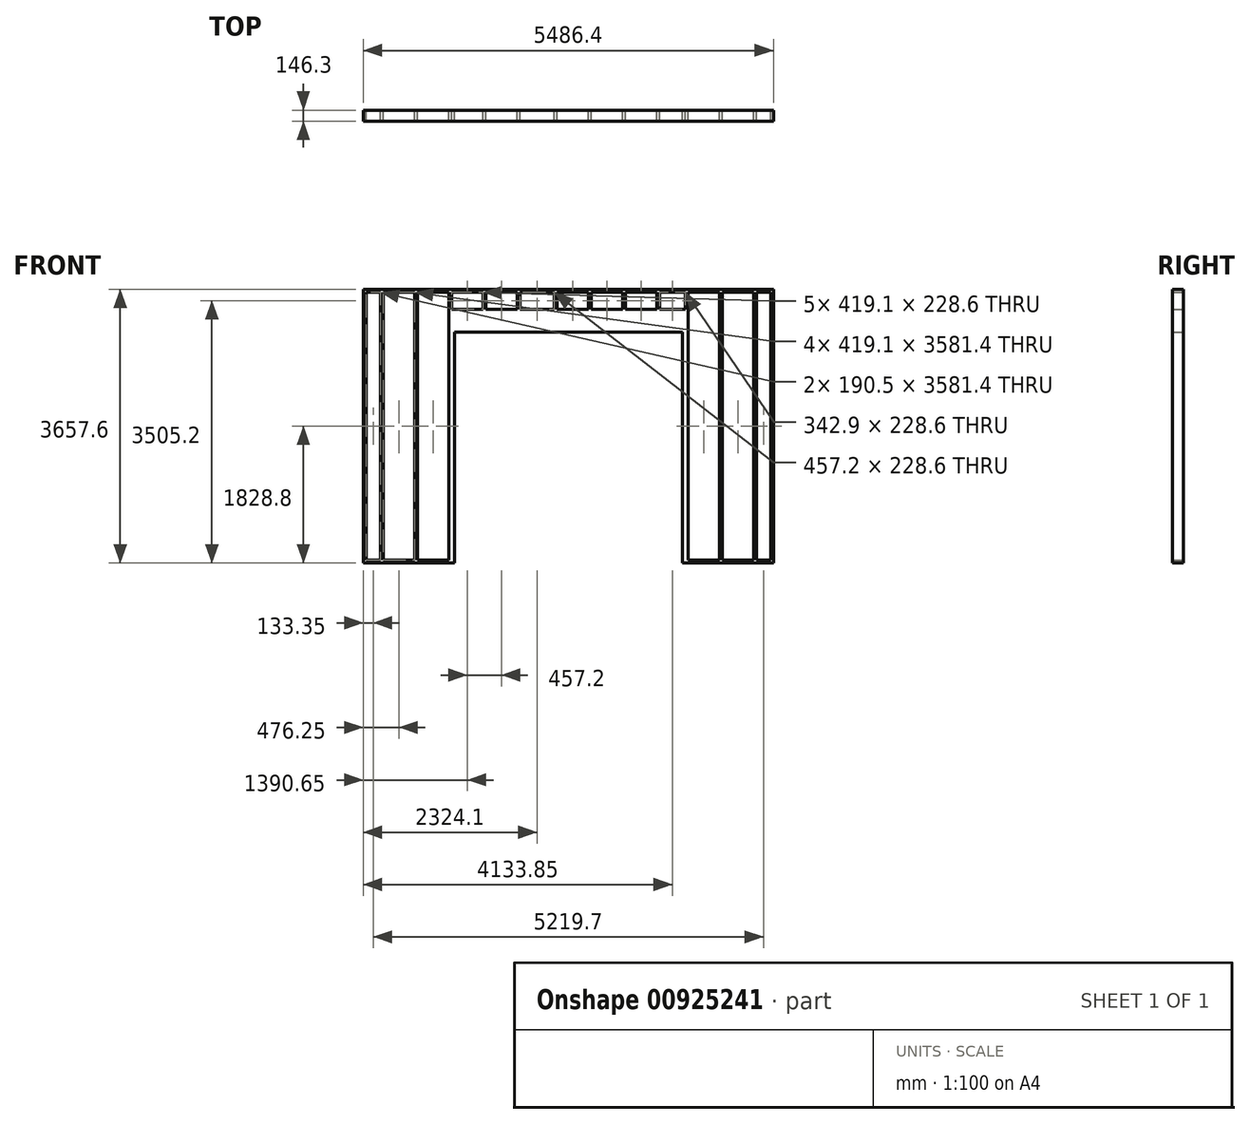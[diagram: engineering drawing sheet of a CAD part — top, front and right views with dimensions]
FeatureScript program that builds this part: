
annotation { "Feature Type Name" : "Feature", "Feature Type Description" : "" }
export const myFeature = defineFeature(function(context is Context, id is Id, definition is map)
    precondition{}
    {
        {
            var Q0;
            Q0=qCreatedBy(makeId("Front.planeOp"),FACE);
            var sketch = newSketch(context, id + "F0", { "sketchPlane" : qUnion([Q0])});
            skLineSegment(sketch, "E0.bottom", {"start": v(822.96, 0) * mm, "end": v(2042.16, 0) * mm});
            skLineSegment(sketch, "E0.top", {"start": v(822.96, 3657.6) * mm, "end": v(6309.36, 3657.6) * mm});
            skLineSegment(sketch, "E1.1.0.0", {"start": v(822.96, 3619.5) * mm, "end": v(822.96, 38.1) * mm});
            skLineSegment(sketch, "E1.1.0.1", {"start": v(861.06, 3619.5) * mm, "end": v(861.06, 38.1) * mm});
            skLineSegment(sketch, "E1.2.0.0", {"start": v(1051.56, 3619.5) * mm, "end": v(1051.56, 38.1) * mm});
            skLineSegment(sketch, "E1.2.0.1", {"start": v(1089.66, 3619.5) * mm, "end": v(1089.66, 38.1) * mm});
            skLineSegment(sketch, "E1.3.0.0", {"start": v(1508.76, 3619.5) * mm, "end": v(1508.76, 38.1) * mm});
            skLineSegment(sketch, "E1.3.0.1", {"start": v(1546.86, 3619.5) * mm, "end": v(1546.86, 38.1) * mm});
            skLineSegment(sketch, "E1.4.0.0", {"start": v(1965.96, 3619.5) * mm, "end": v(1965.96, 38.1) * mm});
            skLineSegment(sketch, "E1.4.0.1", {"start": v(2004.06, 3619.5) * mm, "end": v(2004.06, 3390.9) * mm});
            skLineSegment(sketch, "E1.5.0.0", {"start": v(2423.16, 3619.5) * mm, "end": v(2423.16, 3390.9) * mm});
            skLineSegment(sketch, "E1.5.0.1", {"start": v(2461.26, 3619.5) * mm, "end": v(2461.26, 3390.9) * mm});
            skLineSegment(sketch, "E1.6.0.0", {"start": v(2880.36, 3619.5) * mm, "end": v(2880.36, 3390.9) * mm});
            skLineSegment(sketch, "E1.6.0.1", {"start": v(2918.46, 3619.5) * mm, "end": v(2918.46, 3390.9) * mm});
            skLineSegment(sketch, "E1.7.0.0", {"start": v(3375.66, 3619.5) * mm, "end": v(3375.66, 3390.9) * mm});
            skLineSegment(sketch, "E1.7.0.1", {"start": v(3413.76, 3619.5) * mm, "end": v(3413.76, 3390.9) * mm});
            skLineSegment(sketch, "E1.8.0.0", {"start": v(3832.86, 3619.5) * mm, "end": v(3832.86, 3390.9) * mm});
            skLineSegment(sketch, "E1.8.0.1", {"start": v(3870.96, 3619.5) * mm, "end": v(3870.96, 3390.9) * mm});
            skLineSegment(sketch, "E1.9.0.0", {"start": v(4290.06, 3619.5) * mm, "end": v(4290.06, 3390.9) * mm});
            skLineSegment(sketch, "E1.9.0.1", {"start": v(4328.16, 3619.5) * mm, "end": v(4328.16, 3390.9) * mm});
            skLineSegment(sketch, "E1.10.0.0", {"start": v(4747.26, 3619.5) * mm, "end": v(4747.26, 3390.9) * mm});
            skLineSegment(sketch, "E1.10.0.1", {"start": v(4785.36, 3619.5) * mm, "end": v(4785.36, 3390.9) * mm});
            skLineSegment(sketch, "E1.11.0.0", {"start": v(5128.26, 3619.5) * mm, "end": v(5128.26, 3390.9) * mm});
            skLineSegment(sketch, "E1.11.0.1", {"start": v(5166.36, 3619.5) * mm, "end": v(5166.36, 38.1) * mm});
            skLineSegment(sketch, "E1.12.0.0", {"start": v(5585.46, 3619.5) * mm, "end": v(5585.46, 38.1) * mm});
            skLineSegment(sketch, "E1.12.0.1", {"start": v(5623.56, 3619.5) * mm, "end": v(5623.56, 38.1) * mm});
            skLineSegment(sketch, "E1.13.0.0", {"start": v(6042.66, 3619.5) * mm, "end": v(6042.66, 38.1) * mm});
            skLineSegment(sketch, "E1.13.0.1", {"start": v(6080.76, 3619.5) * mm, "end": v(6080.76, 38.1) * mm});
            skLineSegment(sketch, "E1.14.0.0", {"start": v(6271.26, 3619.5) * mm, "end": v(6271.26, 38.1) * mm});
            skLineSegment(sketch, "E1.14.0.1", {"start": v(6309.36, 3619.5) * mm, "end": v(6309.36, 38.1) * mm});
            skLineSegment(sketch, "E2.trimOffspring", {"start": v(861.06, 3619.5) * mm, "end": v(1051.56, 3619.5) * mm});
            skLineSegment(sketch, "E3.trimOffspring", {"start": v(1089.66, 3619.5) * mm, "end": v(1508.76, 3619.5) * mm});
            skLineSegment(sketch, "E4.trimOffspring", {"start": v(1546.86, 3619.5) * mm, "end": v(1965.96, 3619.5) * mm});
            skLineSegment(sketch, "E5.trimOffspring", {"start": v(2004.06, 3619.5) * mm, "end": v(2423.16, 3619.5) * mm});
            skLineSegment(sketch, "E6.trimOffspring", {"start": v(2461.26, 3619.5) * mm, "end": v(2880.36, 3619.5) * mm});
            skLineSegment(sketch, "E7.trimOffspring", {"start": v(2918.46, 3619.5) * mm, "end": v(3375.66, 3619.5) * mm});
            skLineSegment(sketch, "E8.trimOffspring", {"start": v(3413.76, 3619.5) * mm, "end": v(3832.86, 3619.5) * mm});
            skLineSegment(sketch, "E9.trimOffspring", {"start": v(3870.96, 3619.5) * mm, "end": v(4290.06, 3619.5) * mm});
            skLineSegment(sketch, "E10.trimOffspring", {"start": v(4328.16, 3619.5) * mm, "end": v(4747.26, 3619.5) * mm});
            skLineSegment(sketch, "E11.trimOffspring", {"start": v(4785.36, 3619.5) * mm, "end": v(5128.26, 3619.5) * mm});
            skLineSegment(sketch, "E12.trimOffspring", {"start": v(5166.36, 3619.5) * mm, "end": v(5585.46, 3619.5) * mm});
            skLineSegment(sketch, "E13.trimOffspring", {"start": v(5623.56, 3619.5) * mm, "end": v(6042.66, 3619.5) * mm});
            skLineSegment(sketch, "E14.trimOffspring", {"start": v(6080.76, 3619.5) * mm, "end": v(6271.26, 3619.5) * mm});
            skLineSegment(sketch, "E15.trimOffspring", {"start": v(6080.76, 38.1) * mm, "end": v(6271.26, 38.1) * mm});
            skLineSegment(sketch, "E16.trimOffspring", {"start": v(5623.56, 38.1) * mm, "end": v(6042.66, 38.1) * mm});
            skLineSegment(sketch, "E17.trimOffspring", {"start": v(5166.36, 38.1) * mm, "end": v(5585.46, 38.1) * mm});
            skLineSegment(sketch, "E18.trimOffspring", {"start": v(1546.86, 38.1) * mm, "end": v(1965.96, 38.1) * mm});
            skLineSegment(sketch, "E19.trimOffspring", {"start": v(1089.66, 38.1) * mm, "end": v(1508.76, 38.1) * mm});
            skLineSegment(sketch, "E20.trimOffspring", {"start": v(861.06, 38.1) * mm, "end": v(1051.56, 38.1) * mm});
            skLineSegment(sketch, "E21.top", {"start": v(2042.16, 3086.1) * mm, "end": v(5090.16, 3086.1) * mm});
            skLineSegment(sketch, "E21.left", {"start": v(2042.16, 38.1) * mm, "end": v(2042.16, 3086.1) * mm});
            skLineSegment(sketch, "E21.right", {"start": v(5090.16, 38.1) * mm, "end": v(5090.16, 3086.1) * mm});
            skLineSegment(sketch, "E22", {"start": v(2004.06, 3390.9) * mm, "end": v(2423.16, 3390.9) * mm});
            skLineSegment(sketch, "E23.trimOffspring", {"start": v(2461.26, 3390.9) * mm, "end": v(2880.36, 3390.9) * mm});
            skLineSegment(sketch, "E24.trimOffspring", {"start": v(2918.46, 3390.9) * mm, "end": v(3375.66, 3390.9) * mm});
            skLineSegment(sketch, "E25.trimOffspring", {"start": v(3413.76, 3390.9) * mm, "end": v(3832.86, 3390.9) * mm});
            skLineSegment(sketch, "E26.trimOffspring", {"start": v(3870.96, 3390.9) * mm, "end": v(4290.06, 3390.9) * mm});
            skLineSegment(sketch, "E27.trimOffspring", {"start": v(4328.16, 3390.9) * mm, "end": v(4747.26, 3390.9) * mm});
            skLineSegment(sketch, "E28.trimOffspring", {"start": v(4785.36, 3390.9) * mm, "end": v(5128.26, 3390.9) * mm});
            skLineSegment(sketch, "E29", {"start": v(2042.16, 38.1) * mm, "end": v(2042.16, 0) * mm});
            skLineSegment(sketch, "E30", {"start": v(5090.16, 38.1) * mm, "end": v(5090.16, 0) * mm});
            skLineSegment(sketch, "E31.trimOffspring", {"start": v(5090.16, 0) * mm, "end": v(6309.36, 0) * mm});
            skLineSegment(sketch, "E32", {"start": v(6309.36, 3619.5) * mm, "end": v(6309.36, 3657.6) * mm});
            skLineSegment(sketch, "E33", {"start": v(6309.36, 38.1) * mm, "end": v(6309.36, 0) * mm});
            skLineSegment(sketch, "E34", {"start": v(822.96, 3619.5) * mm, "end": v(822.96, 3657.6) * mm});
            skLineSegment(sketch, "E35", {"start": v(822.96, 38.1) * mm, "end": v(822.96, 0) * mm});
            skSolve(sketch);
        }
        {
            var Q0;
            Q0=qSketchRegion(id+"F0",true);
            extrude(context, id + "F1", {"entities" : qUnion([Q0]), "depth" : 146.3 * mm, "offsetDistance" : 30.48 * mm});
        }
    });
